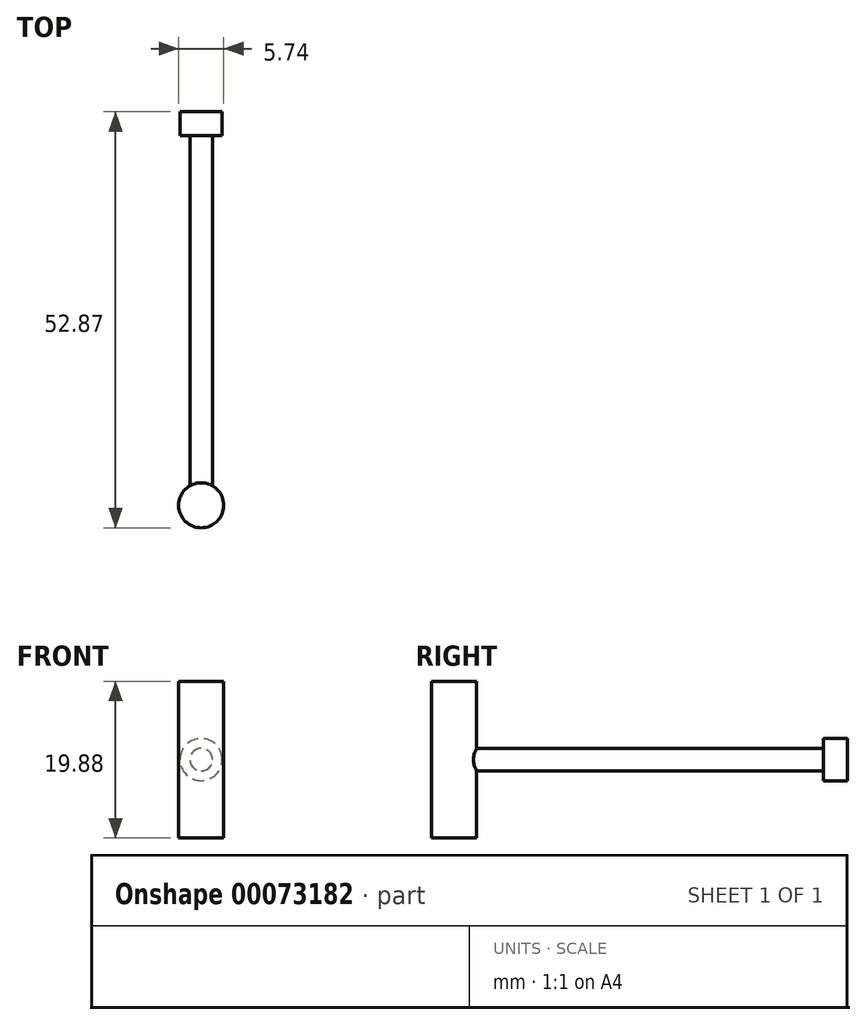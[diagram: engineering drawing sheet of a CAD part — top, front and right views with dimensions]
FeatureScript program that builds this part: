
annotation { "Feature Type Name" : "Feature", "Feature Type Description" : "" }
export const myFeature = defineFeature(function(context is Context, id is Id, definition is map)
    precondition{}
    {
        {
            var Q0;
            Q0=qCreatedBy(makeId("Top.planeOp"),FACE);
            var sketch = newSketch(context, id + "F0", { "sketchPlane" : qUnion([Q0])});
            skCircle(sketch, "E0", {"center": v(0, 0) * mm, "radius": 2.87 * mm});
            skSolve(sketch);
        }
        {
            var Q0;
            Q0 = qSketchRegion(id + "F0", true);
            extrude(context, id + "F1", {"entities" : qUnion([Q0]), "depth" : 19.88 * mm});
        }
        {
            var Q0;
            Q0=qCreatedBy(makeId("Right.planeOp"),FACE);
            var sketch = newSketch(context, id + "F2", { "sketchPlane" : qUnion([Q0])});
            skLineSegment(sketch, "E1", {"start": v(0, 0) * mm, "end": v(0, 19.88) * mm, "construction": true});
            skLineSegment(sketch, "E2", {"start": v(0, 9.94) * mm, "end": v(25.72, 9.94) * mm, "construction": true});
            skSolve(sketch);
        }
        {
            var Q0;
            Q0=qCreatedBy(makeId("Front.planeOp"),FACE);
            var sketch = newSketch(context, id + "F3", { "sketchPlane" : qUnion([Q0])});
            skCircle(sketch, "E3", {"center": v(0, 9.94) * mm, "radius": 1.44 * mm});
            skSolve(sketch);
        }
        {
            var Q0;
            Q0 = qSketchRegion(id + "F3", true);
            extrude(context, id + "F4", {"entities" : qUnion([Q0]), "operationType" : NewBodyOperationType.ADD, "oppositeDirection" : true, "depth" : 50 * mm});
        }
        {
            var Q0;
            Q0=makeQuery(id+"F4.opExtrude","CAP_FACE",FACE,{"disambiguationData":[OSD([sQuery(id+"F3.wireOp",EDGE,"E3")])],"isStart":false});
            var sketch = newSketch(context, id + "F5", { "sketchPlane" : qUnion([Q0])});
            skCircle(sketch, "E4", {"center": v(0, 9.94) * mm, "radius": 2.67 * mm});
            skSolve(sketch);
        }
        {
            var Q0;
            Q0=makeQuery(id+"F5.imprint","IMPRINT",FACE,{"disambiguationData":[TD([[makeQuery(id+"F5.imprint","IMPRINT",EDGE,{"derivedFrom":sQuery(id+"F5.wireOp",EDGE,"E4")}),1.0]])]});
            extrude(context, id + "F6", {"entities" : qUnion([Q0]), "operationType" : NewBodyOperationType.ADD, "oppositeDirection" : true, "depth" : 3.06 * mm});
        }
    });
